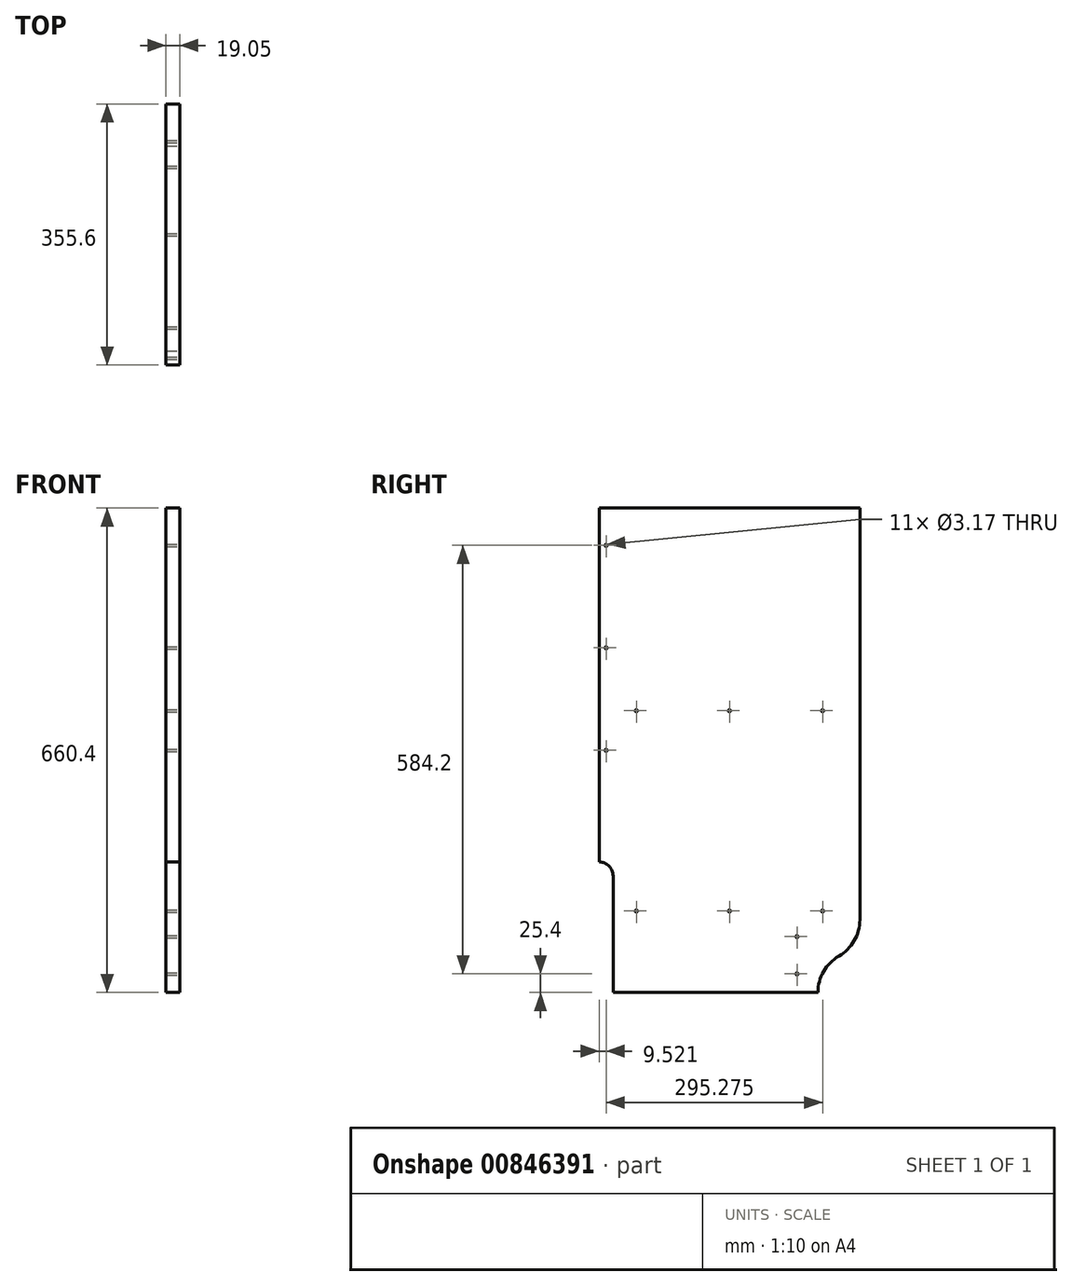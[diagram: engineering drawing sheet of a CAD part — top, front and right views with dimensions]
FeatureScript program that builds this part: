
annotation { "Feature Type Name" : "Feature", "Feature Type Description" : "" }
export const myFeature = defineFeature(function(context is Context, id is Id, definition is map)
    precondition{}
    {
        {
            var Q0;
            Q0=qCreatedBy(makeId("Right.planeOp"),FACE);
            var sketch = newSketch(context, id + "F0", { "sketchPlane" : qUnion([Q0])});
            skLineSegment(sketch, "E0.bottom", {"start": v(-155.23, 482.6) * mm, "end": v(200.37, 482.6) * mm});
            skLineSegment(sketch, "E0.top", {"start": v(-136.18, -177.8) * mm, "end": v(143.22, -177.8) * mm});
            skLineSegment(sketch, "E0.left", {"start": v(-155.23, 482.6) * mm, "end": v(-155.23, 0) * mm});
            skLineSegment(sketch, "E0.right", {"start": v(200.37, 482.6) * mm, "end": v(200.37, -78.81) * mm});
            skArc(sketch, "E1", {"start": v(171.8, -128.3) * mm, "mid": v(150.87, -149.22) * mm, "end": v(143.22, -177.8) * mm});
            skLineSegment(sketch, "E2.top", {"start": v(-155.23, 0) * mm, "end": v(-155.23, 0) * mm});
            skLineSegment(sketch, "E2.right", {"start": v(-136.18, -177.8) * mm, "end": v(-136.18, -19.05) * mm});
            skPoint(sketch, "E3.visualSharp", {"position": v(-136.18, 0) * mm});
            skArc(sketch, "E3.filletArc", {"start": v(-136.18, -19.05) * mm, "mid": v(-141.76, -5.58) * mm, "end": v(-155.23, 0) * mm});
            skArc(sketch, "E4.filletArc", {"start": v(171.8, -128.3) * mm, "mid": v(192.7, -107.39) * mm, "end": v(200.37, -78.81) * mm});
            skCircle(sketch, "E5", {"center": v(-145.7, 431.8) * mm, "radius": 1.59 * mm});
            skCircle(sketch, "E6", {"center": v(-145.7, 292.1) * mm, "radius": 1.59 * mm});
            skCircle(sketch, "E7", {"center": v(-145.7, 152.4) * mm, "radius": 1.59 * mm});
            skCircle(sketch, "E8", {"center": v(149.57, -66.67) * mm, "radius": 1.59 * mm});
            skCircle(sketch, "E9", {"center": v(22.57, -66.67) * mm, "radius": 1.59 * mm});
            skCircle(sketch, "E10", {"center": v(-104.43, -66.67) * mm, "radius": 1.59 * mm});
            skCircle(sketch, "E11", {"center": v(149.57, 206.38) * mm, "radius": 1.59 * mm});
            skCircle(sketch, "E12", {"center": v(22.57, 206.38) * mm, "radius": 1.59 * mm});
            skCircle(sketch, "E13", {"center": v(-104.43, 206.38) * mm, "radius": 1.59 * mm});
            skCircle(sketch, "E14", {"center": v(114.64, -101.6) * mm, "radius": 1.59 * mm});
            skCircle(sketch, "E15", {"center": v(114.64, -152.4) * mm, "radius": 1.59 * mm});
            skSolve(sketch);
        }
        {
            var Q0;
            Q0 = qSketchRegion(id + "F0", true);
            extrude(context, id + "F1", {"entities" : qUnion([Q0]), "oppositeDirection" : true, "depth" : 19.05 * mm, "offsetDistance" : 25.4 * mm});
        }
    });
